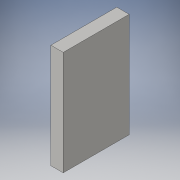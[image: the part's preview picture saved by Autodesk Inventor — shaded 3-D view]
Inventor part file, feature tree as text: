
AUTODESK INVENTOR PART (.ipt)
format: ipt  version: 2016 (Build 200138000, 138)  size: 84,992 bytes
history: native  units: in
note: dims shown in document units (in); Inventor stores cm internally (conversion verified against a paired STEP export)
features: extrude x1, sketch x1
ambient origin geometry x8: Origin, YZ Plane, XZ Plane, XY Plane, X Axis, Y Axis, Z Axis, Center Point
bodies: Solid1 (feature_tree)
feature tree (2):
  extrude  "Extrusion1"  Depth=4.0in
  sketch  "Sketch1"  dims[d0=6.33in d1=4.0in d2=0.75in d3=0.0in]
